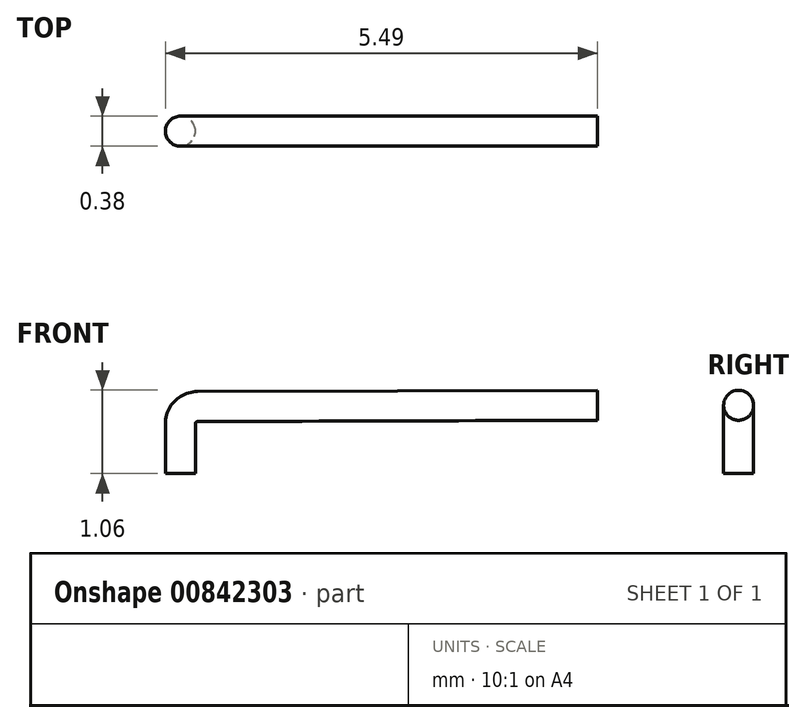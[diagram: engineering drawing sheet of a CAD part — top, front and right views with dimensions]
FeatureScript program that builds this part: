
annotation { "Feature Type Name" : "Feature", "Feature Type Description" : "" }
export const myFeature = defineFeature(function(context is Context, id is Id, definition is map)
    precondition{}
    {
        {
            var Q0;
            Q0=qCreatedBy(makeId("Top.planeOp"),FACE);
            var sketch = newSketch(context, id + "F0", { "sketchPlane" : qUnion([Q0])});
            skCircle(sketch, "E0", {"center": v(0, 0) * mm, "radius": 0.2 * mm});
            skSolve(sketch);
        }
        {
            var Q0;
            Q0=qCreatedBy(makeId("Front.planeOp"),FACE);
            var sketch = newSketch(context, id + "F1", { "sketchPlane" : qUnion([Q0])});
            skLineSegment(sketch, "E1", {"start": v(0, 0) * mm, "end": v(0, 0.63) * mm});
            skArc(sketch, "E2", {"start": v(0, 0.64) * mm, "mid": v(0.06, 0.79) * mm, "end": v(0.22, 0.85) * mm});
            skLineSegment(sketch, "E3", {"start": v(0.22, 0.85) * mm, "end": v(5.3, 0.87) * mm});
            skSolve(sketch);
        }
        {
            var Q0;
            Q0=makeQuery(id+"F0.imprint","IMPRINT",FACE,{"disambiguationData":[TD([[makeQuery(id+"F0.imprint","IMPRINT",EDGE,{"derivedFrom":sQuery(id+"F0.wireOp",EDGE,"E0")}),1.0]])]});
            var Q1;
            Q1 = qConstructionFilter(qBodyType(qCreatedBy(id + "F1" ,EDGE), BodyType.WIRE), ConstructionObject.NO);
            sweep(context, id + "F2", {"profiles" : qUnion([Q0]), "path" : qUnion([Q1])});
        }
    });
